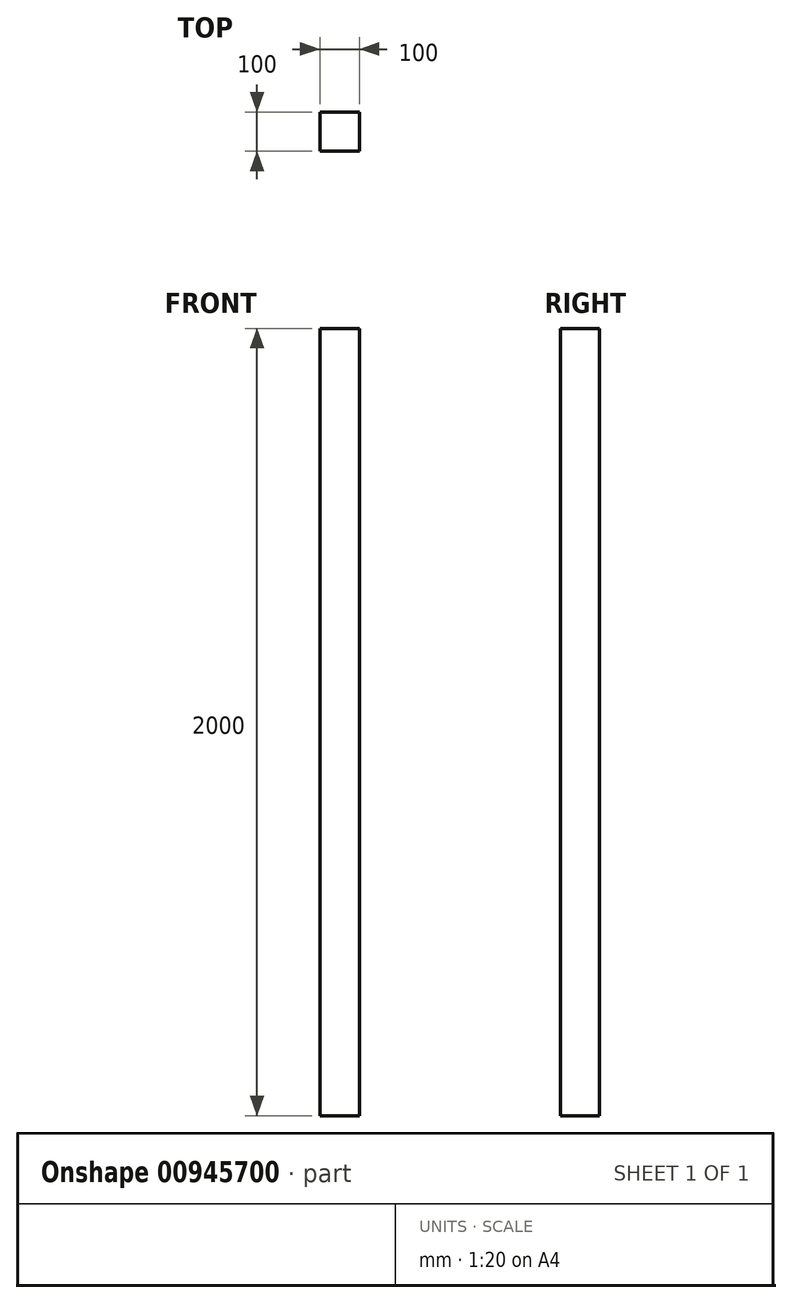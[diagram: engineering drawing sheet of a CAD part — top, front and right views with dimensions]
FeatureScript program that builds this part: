
annotation { "Feature Type Name" : "Feature", "Feature Type Description" : "" }
export const myFeature = defineFeature(function(context is Context, id is Id, definition is map)
    precondition{}
    {
        {
            var Q0;
            Q0=qCreatedBy(makeId("Front.planeOp"),FACE);
            var sketch = newSketch(context, id + "F0", { "sketchPlane" : qUnion([Q0])});
            skLineSegment(sketch, "E0.bottom", {"start": v(50, 1000) * mm, "end": v(-50, 1000) * mm});
            skLineSegment(sketch, "E0.top", {"start": v(50, -1000) * mm, "end": v(-50, -1000) * mm});
            skLineSegment(sketch, "E0.left", {"start": v(50, 1000) * mm, "end": v(50, -1000) * mm});
            skLineSegment(sketch, "E0.right", {"start": v(-50, 1000) * mm, "end": v(-50, -1000) * mm});
            skPoint(sketch, "E0.middle", {"position": v(0, 0) * mm});
            skSolve(sketch);
        }
        {
            var Q0;
            Q0=makeQuery(id+"F0.imprint","IMPRINT",FACE,{"disambiguationData":[TD([[makeQuery(id+"F0.imprint","IMPRINT",EDGE,{"derivedFrom":sQuery(id+"F0.wireOp",EDGE,"E0.bottom")}),1.0]])]});
            extrude(context, id + "F1", {"entities" : qUnion([Q0]), "depth" : 100 * mm, "offsetDistance" : 25 * mm});
        }
    });
